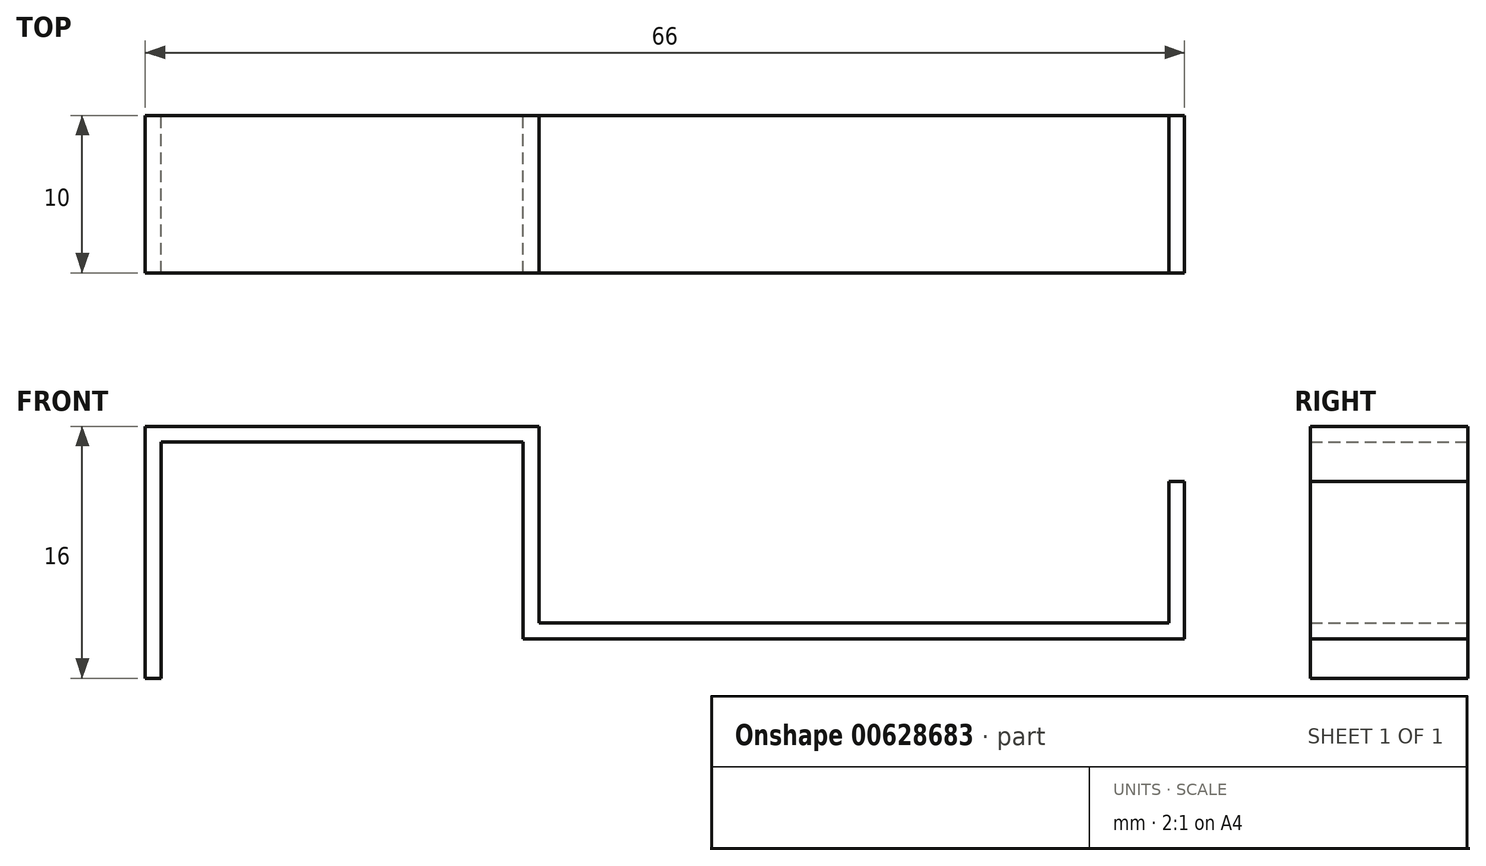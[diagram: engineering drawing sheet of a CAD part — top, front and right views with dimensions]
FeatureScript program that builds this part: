
annotation { "Feature Type Name" : "Feature", "Feature Type Description" : "" }
export const myFeature = defineFeature(function(context is Context, id is Id, definition is map)
    precondition{}
    {
        {
            var Q0;
            Q0=qCreatedBy(makeId("Front.planeOp"),FACE);
            var sketch = newSketch(context, id + "F0", { "sketchPlane" : qUnion([Q0])});
            skLineSegment(sketch, "E0", {"start": v(0, 0) * mm, "end": v(0, 16) * mm});
            skLineSegment(sketch, "E1", {"start": v(0, 16) * mm, "end": v(25, 16) * mm});
            skLineSegment(sketch, "E2", {"start": v(25, 16) * mm, "end": v(25, 3.5) * mm});
            skLineSegment(sketch, "E3", {"start": v(25, 3.5) * mm, "end": v(65, 3.5) * mm});
            skLineSegment(sketch, "E4", {"start": v(65, 3.5) * mm, "end": v(65, 12.5) * mm});
            skLineSegment(sketch, "E5", {"start": v(65, 12.5) * mm, "end": v(66, 12.5) * mm});
            skLineSegment(sketch, "E6", {"start": v(66, 12.5) * mm, "end": v(66, 2.5) * mm});
            skLineSegment(sketch, "E7", {"start": v(66, 2.5) * mm, "end": v(24, 2.5) * mm});
            skLineSegment(sketch, "E8", {"start": v(24, 2.5) * mm, "end": v(24, 15) * mm});
            skLineSegment(sketch, "E9", {"start": v(24, 15) * mm, "end": v(1, 15) * mm});
            skLineSegment(sketch, "E10", {"start": v(1, 15) * mm, "end": v(1, 0) * mm});
            skLineSegment(sketch, "E11", {"start": v(1, 0) * mm, "end": v(0, 0) * mm});
            skSolve(sketch);
        }
        {
            var Q0;
            Q0=makeQuery(id+"F0.imprint","IMPRINT",FACE,{"disambiguationData":[TD([[makeQuery(id+"F0.imprint","IMPRINT",EDGE,{"derivedFrom":sQuery(id+"F0.wireOp",EDGE,"E0")}),-1.0]])]});
            extrude(context, id + "F1", {"entities" : qUnion([Q0]), "depth" : 10 * mm, "offsetDistance" : 25 * mm});
        }
    });
